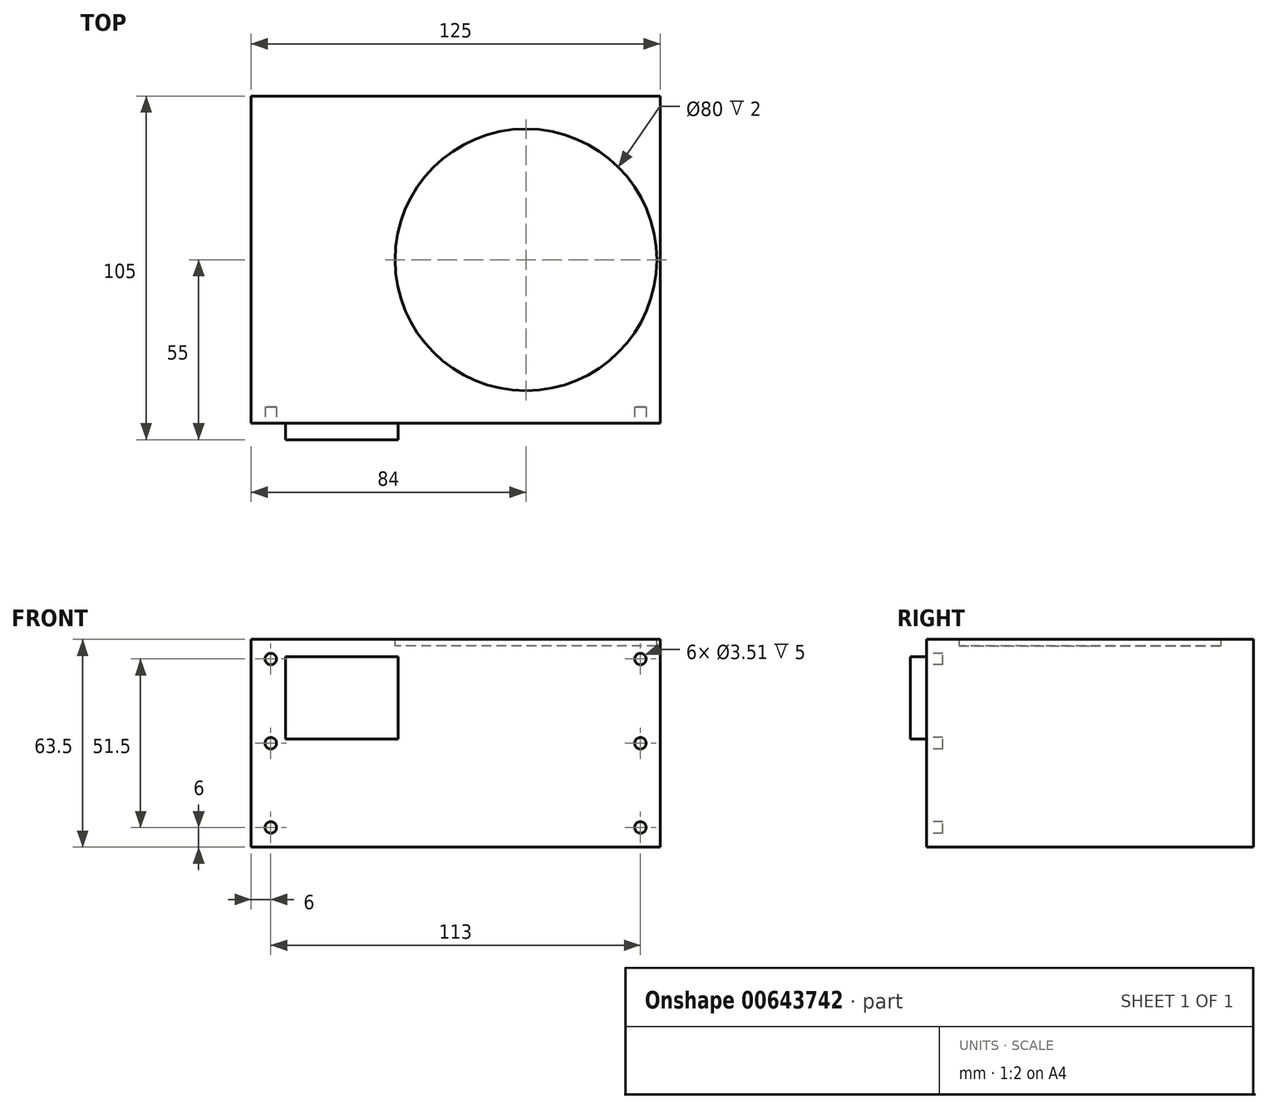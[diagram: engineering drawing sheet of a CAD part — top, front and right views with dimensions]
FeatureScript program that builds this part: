
annotation { "Feature Type Name" : "Feature", "Feature Type Description" : "" }
export const myFeature = defineFeature(function(context is Context, id is Id, definition is map)
    precondition{}
    {
        {
            var Q0;
            Q0=qCreatedBy(makeId("Front.planeOp"),FACE);
            var sketch = newSketch(context, id + "F0", { "sketchPlane" : qUnion([Q0])});
            skLineSegment(sketch, "E0.bottom", {"start": v(62.5, 31.75) * mm, "end": v(-62.5, 31.75) * mm});
            skLineSegment(sketch, "E0.top", {"start": v(62.5, -31.75) * mm, "end": v(-62.5, -31.75) * mm});
            skLineSegment(sketch, "E0.left", {"start": v(62.5, 31.75) * mm, "end": v(62.5, -31.75) * mm});
            skLineSegment(sketch, "E0.right", {"start": v(-62.5, 31.75) * mm, "end": v(-62.5, -31.75) * mm});
            skPoint(sketch, "E0.middle", {"position": v(0, 0) * mm});
            skCircle(sketch, "E1", {"center": v(-56.5, 25.75) * mm, "radius": 1.75 * mm});
            skCircle(sketch, "E2", {"center": v(-56.5, -25.75) * mm, "radius": 1.75 * mm});
            skCircle(sketch, "E3", {"center": v(56.5, 0) * mm, "radius": 1.75 * mm});
            skCircle(sketch, "E4", {"center": v(56.5, 25.75) * mm, "radius": 1.75 * mm});
            skCircle(sketch, "E5", {"center": v(56.5, -25.75) * mm, "radius": 1.75 * mm});
            skCircle(sketch, "E6", {"center": v(-56.5, 0) * mm, "radius": 1.75 * mm});
            skLineSegment(sketch, "E7.bottom", {"start": v(-51.93, 1.25) * mm, "end": v(-17.63, 1.25) * mm});
            skLineSegment(sketch, "E7.top", {"start": v(-51.93, 26.48) * mm, "end": v(-17.63, 26.48) * mm});
            skLineSegment(sketch, "E7.left", {"start": v(-51.93, 1.25) * mm, "end": v(-51.93, 26.48) * mm});
            skLineSegment(sketch, "E7.right", {"start": v(-17.63, 1.25) * mm, "end": v(-17.63, 26.48) * mm});
            skSolve(sketch);
        }
        {
            var Q0;
            Q0=makeQuery(id+"F0.imprint","IMPRINT",FACE,{"disambiguationData":[TD([[makeQuery(id+"F0.imprint","IMPRINT",EDGE,{"derivedFrom":sQuery(id+"F0.wireOp",EDGE,"E0.bottom")}),1.0]])]});
            var Q1;
            Q1=makeQuery(id+"F0.imprint","IMPRINT",FACE,{"disambiguationData":[TD([[makeQuery(id+"F0.imprint","IMPRINT",EDGE,{"derivedFrom":sQuery(id+"F0.wireOp",EDGE,"mgTTsKbE-n987-F8mL-3NHE-uWv0eW6xJJbe.bottom")}),-1.0]])]});
            var Q2;
            Q2=makeQuery(id+"F0.imprint","IMPRINT",FACE,{"disambiguationData":[TD([[makeQuery(id+"F0.imprint","IMPRINT",EDGE,{"derivedFrom":sQuery(id+"F0.wireOp",EDGE,"wuxVYJct-bSm7-f1gI-JZgx-YFrJw5StZBBs.bottom")}),-1.0]])]});
            var Q3;
            Q3=makeQuery(id+"F0.imprint","IMPRINT",FACE,{"disambiguationData":[TD([[makeQuery(id+"F0.imprint","IMPRINT",EDGE,{"derivedFrom":sQuery(id+"F0.wireOp",EDGE,"E7.bottom")}),1.0]])]});
            var Q4;
            Q4=makeQuery(id+"F0.imprint","IMPRINT",FACE,{"disambiguationData":[TD([[makeQuery(id+"F0.imprint","IMPRINT",EDGE,{"derivedFrom":sQuery(id+"F0.wireOp",EDGE,"E1")}),1.0]])]});
            var Q5;
            Q5=makeQuery(id+"F0.imprint","IMPRINT",FACE,{"disambiguationData":[TD([[makeQuery(id+"F0.imprint","IMPRINT",EDGE,{"derivedFrom":sQuery(id+"F0.wireOp",EDGE,"E6")}),1.0]])]});
            var Q6;
            Q6=makeQuery(id+"F0.imprint","IMPRINT",FACE,{"disambiguationData":[TD([[makeQuery(id+"F0.imprint","IMPRINT",EDGE,{"derivedFrom":sQuery(id+"F0.wireOp",EDGE,"E2")}),1.0]])]});
            var Q7;
            Q7=makeQuery(id+"F0.imprint","IMPRINT",FACE,{"disambiguationData":[TD([[makeQuery(id+"F0.imprint","IMPRINT",EDGE,{"derivedFrom":sQuery(id+"F0.wireOp",EDGE,"E5")}),1.0]])]});
            var Q8;
            Q8=makeQuery(id+"F0.imprint","IMPRINT",FACE,{"disambiguationData":[TD([[makeQuery(id+"F0.imprint","IMPRINT",EDGE,{"derivedFrom":sQuery(id+"F0.wireOp",EDGE,"E3")}),1.0]])]});
            var Q9;
            Q9=makeQuery(id+"F0.imprint","IMPRINT",FACE,{"disambiguationData":[TD([[makeQuery(id+"F0.imprint","IMPRINT",EDGE,{"derivedFrom":sQuery(id+"F0.wireOp",EDGE,"E4")}),1.0]])]});
            extrude(context, id + "F1", {"entities" : qUnion([Q0, Q1, Q2, Q3, Q4, Q5, Q6, Q7, Q8, Q9]), "depth" : -100 * mm, "offsetDistance" : 25 * mm});
        }
        {
            var Q0;
            Q0=makeQuery(id+"F0.imprint","IMPRINT",FACE,{"disambiguationData":[TD([[makeQuery(id+"F0.imprint","IMPRINT",EDGE,{"derivedFrom":sQuery(id+"F0.wireOp",EDGE,"E7.bottom")}),1.0]])]});
            extrude(context, id + "F2", {"entities" : qUnion([Q0]), "operationType" : NewBodyOperationType.ADD, "depth" : 5 * mm, "offsetDistance" : 25 * mm});
        }
        {
            var Q0;
            Q0=makeQuery(id+"F0.imprint","IMPRINT",FACE,{"disambiguationData":[TD([[makeQuery(id+"F0.imprint","IMPRINT",EDGE,{"derivedFrom":sQuery(id+"F0.wireOp",EDGE,"E1")}),1.0]])]});
            var Q1;
            Q1=makeQuery(id+"F0.imprint","IMPRINT",FACE,{"disambiguationData":[TD([[makeQuery(id+"F0.imprint","IMPRINT",EDGE,{"derivedFrom":sQuery(id+"F0.wireOp",EDGE,"E6")}),1.0]])]});
            var Q2;
            Q2=makeQuery(id+"F0.imprint","IMPRINT",FACE,{"disambiguationData":[TD([[makeQuery(id+"F0.imprint","IMPRINT",EDGE,{"derivedFrom":sQuery(id+"F0.wireOp",EDGE,"E2")}),1.0]])]});
            var Q3;
            Q3=makeQuery(id+"F0.imprint","IMPRINT",FACE,{"disambiguationData":[TD([[makeQuery(id+"F0.imprint","IMPRINT",EDGE,{"derivedFrom":sQuery(id+"F0.wireOp",EDGE,"E5")}),1.0]])]});
            var Q4;
            Q4=makeQuery(id+"F0.imprint","IMPRINT",FACE,{"disambiguationData":[TD([[makeQuery(id+"F0.imprint","IMPRINT",EDGE,{"derivedFrom":sQuery(id+"F0.wireOp",EDGE,"E3")}),1.0]])]});
            var Q5;
            Q5=makeQuery(id+"F0.imprint","IMPRINT",FACE,{"disambiguationData":[TD([[makeQuery(id+"F0.imprint","IMPRINT",EDGE,{"derivedFrom":sQuery(id+"F0.wireOp",EDGE,"E4")}),1.0]])]});
            extrude(context, id + "F3", {"entities" : qUnion([Q0, Q1, Q2, Q3, Q4, Q5]), "operationType" : NewBodyOperationType.REMOVE, "oppositeDirection" : true, "depth" : 5 * mm, "offsetDistance" : 25 * mm});
        }
        {
            var Q0;
            Q0=makeQuery(id+"F1.opExtrude","SWEPT_FACE",FACE,{"disambiguationData":[OSD([sQuery(id+"F0.wireOp",EDGE,"E0.bottom")])]});
            var sketch = newSketch(context, id + "F4", { "sketchPlane" : qUnion([Q0])});
            skCircle(sketch, "E8", {"center": v(21.5, 50) * mm, "radius": 40 * mm});
            skSolve(sketch);
        }
        {
            var Q0;
            Q0=makeQuery(id+"F4.imprint","IMPRINT",FACE,{"disambiguationData":[TD([[makeQuery(id+"F4.imprint","IMPRINT",EDGE,{"derivedFrom":sQuery(id+"F4.wireOp",EDGE,"E8")}),1.0]])]});
            extrude(context, id + "F5", {"entities" : qUnion([Q0]), "operationType" : NewBodyOperationType.REMOVE, "oppositeDirection" : true, "depth" : 2 * mm, "offsetDistance" : 25 * mm});
        }
    });
